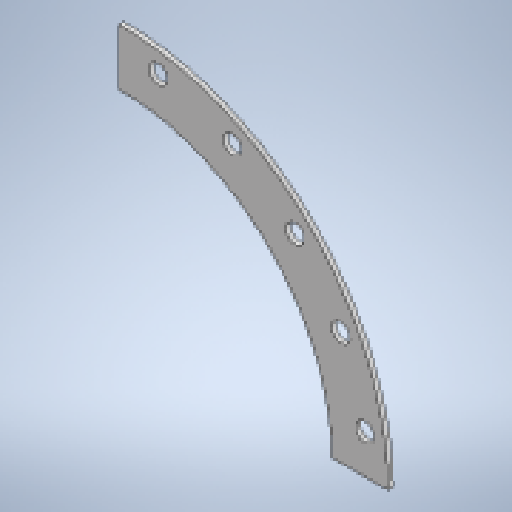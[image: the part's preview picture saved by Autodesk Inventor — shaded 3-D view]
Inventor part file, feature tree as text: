
AUTODESK INVENTOR PART (.ipt)
format: ipt  version: 2025.1 (Build 291241020, 241B)  size: 208,896 bytes
history: native  units: mm
features: sketch x2, other x2, extrude x1, pattern_circular x1, projected_geometry x1
ambient origin geometry x8: Origin, YZ Plane, XZ Plane, XY Plane, X Axis, Y Axis, Z Axis, Center Point
bodies: Solid1 (feature_tree)
feature tree (7):
  extrude  "Extrusion1"  Depth=6.0mm TaperAngle=0.0deg
  pattern_circular  "Circular Pattern1"  Count=53  [1 undecoded]
  sketch  "Sketch1"  dims[d0=512.0mm d1=670.0mm d2=6.0mm d3=0.0mm d4=530.0mm]
  sketch  "Sketch2"  dims[d5=310.0mm d6=1.570796mm d7=23.0mm d8=8.0mm d9=8.0mm d10=0.0mm d11=200.0mm d12=360.0deg]
  projected_geometry  "Projected Loop1"
  other  "Cut1"
  other  "Definition1"
note: 1 required parameter value undecoded (feature->parameter linkage not recoverable at this tier; creation-order binding heuristic only, values carry confidence <= 0.55)
